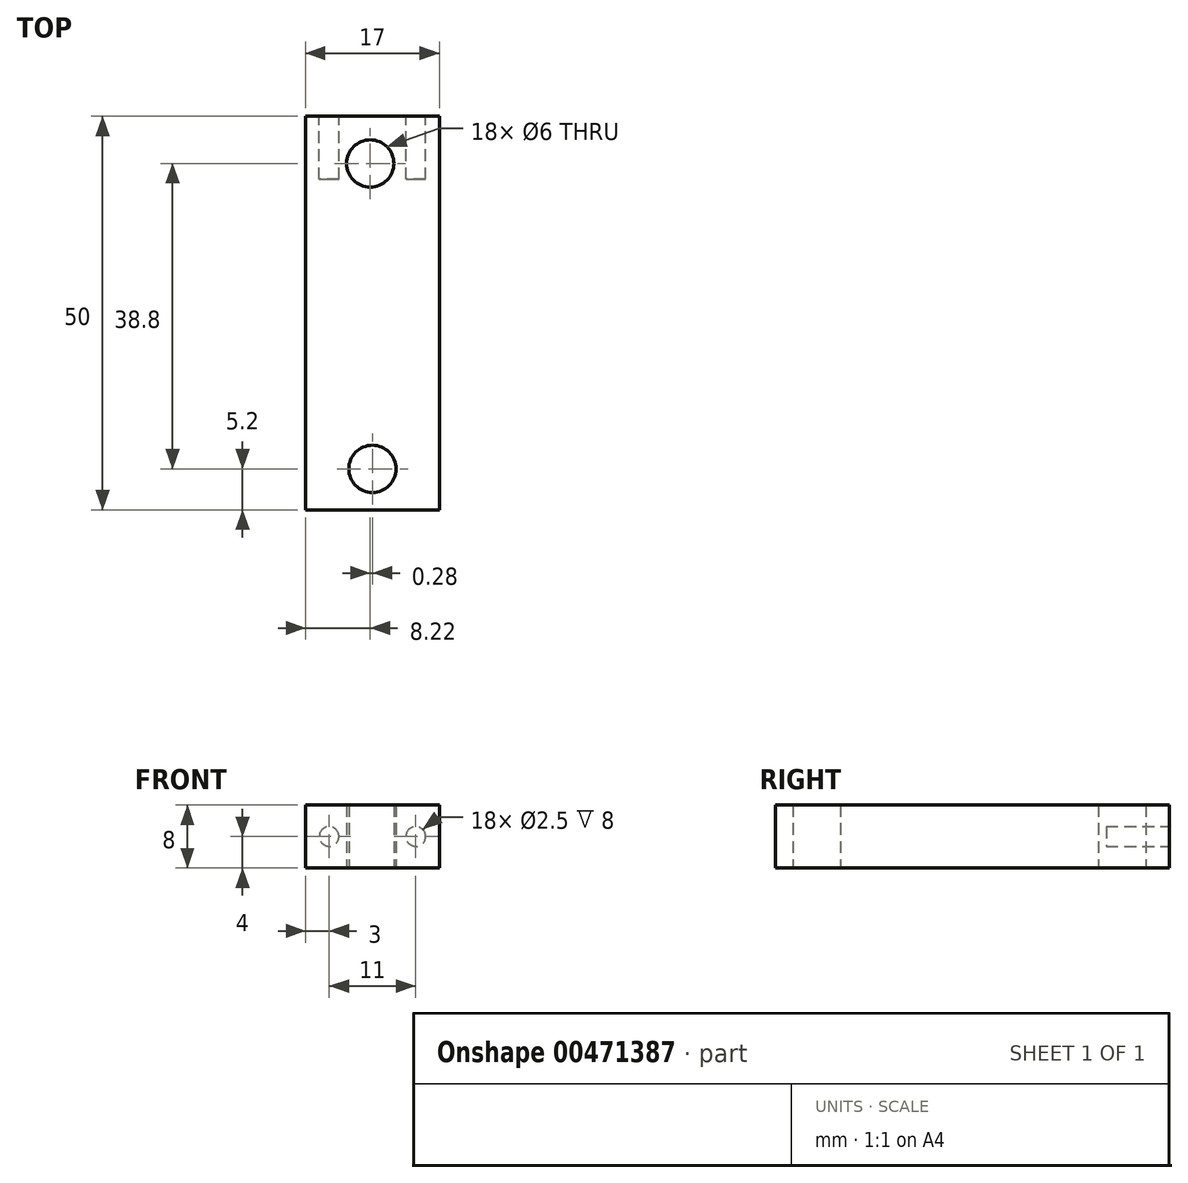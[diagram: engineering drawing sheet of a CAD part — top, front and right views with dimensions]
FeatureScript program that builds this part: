
annotation { "Feature Type Name" : "Feature", "Feature Type Description" : "" }
export const myFeature = defineFeature(function(context is Context, id is Id, definition is map)
    precondition{}
    {
        {
            var Q0;
            Q0=qCreatedBy(makeId("Top.planeOp"),FACE);
            var sketch = newSketch(context, id + "F0", { "sketchPlane" : qUnion([Q0])});
            skLineSegment(sketch, "E0.bottom", {"start": v(0, 0) * mm, "end": v(17, 0) * mm});
            skLineSegment(sketch, "E0.top", {"start": v(0, 50) * mm, "end": v(17, 50) * mm});
            skLineSegment(sketch, "E0.left", {"start": v(0, 0) * mm, "end": v(0, 50) * mm});
            skLineSegment(sketch, "E0.right", {"start": v(17, 0) * mm, "end": v(17, 50) * mm});
            skCircle(sketch, "E1", {"center": v(8.5, 5.2) * mm, "radius": 3 * mm});
            skPoint(sketch, "E1.centerSnap0", {"position": v(8.5, 0) * mm});
            skCircle(sketch, "E2", {"center": v(8.22, 44) * mm, "radius": 3 * mm});
            skSolve(sketch);
        }
        {
            var Q0;
            Q0=makeQuery(id+"F0.imprint","IMPRINT",FACE,{"disambiguationData":[TD([[makeQuery(id+"F0.imprint","IMPRINT",EDGE,{"derivedFrom":sQuery(id+"F0.wireOp",EDGE,"E0.bottom")}),1.0]])]});
            extrude(context, id + "F1", {"entities" : qUnion([Q0]), "depth" : 8 * mm});
        }
        {
            var Q0;
            Q0=makeQuery(id+"F1.opExtrude","SWEPT_FACE",FACE,{"disambiguationData":[OSD([sQuery(id+"F0.wireOp",EDGE,"E0.top")])]});
            var sketch = newSketch(context, id + "F2", { "sketchPlane" : qUnion([Q0])});
            skCircle(sketch, "E3", {"center": v(-14, 4) * mm, "radius": 1.25 * mm});
            skPoint(sketch, "E3.centerSnap0", {"position": v(-17, 4) * mm});
            skPoint(sketch, "E3.perimeterSnap0", {"position": v(-17, 4) * mm});
            skCircle(sketch, "E4", {"center": v(-3, 4) * mm, "radius": 1.25 * mm});
            skSolve(sketch);
        }
        {
            var Q0;
            Q0=makeQuery(id+"F2.imprint","IMPRINT",FACE,{"disambiguationData":[TD([[makeQuery(id+"F2.imprint","IMPRINT",EDGE,{"derivedFrom":sQuery(id+"F2.wireOp",EDGE,"E3")}),1.0]])]});
            var Q1;
            Q1=makeQuery(id+"F2.imprint","IMPRINT",FACE,{"disambiguationData":[TD([[makeQuery(id+"F2.imprint","IMPRINT",EDGE,{"derivedFrom":sQuery(id+"F2.wireOp",EDGE,"E4")}),1.0]])]});
            extrude(context, id + "F3", {"entities" : qUnion([Q0, Q1]), "operationType" : NewBodyOperationType.REMOVE, "oppositeDirection" : true, "depth" : 8 * mm});
        }
    });
